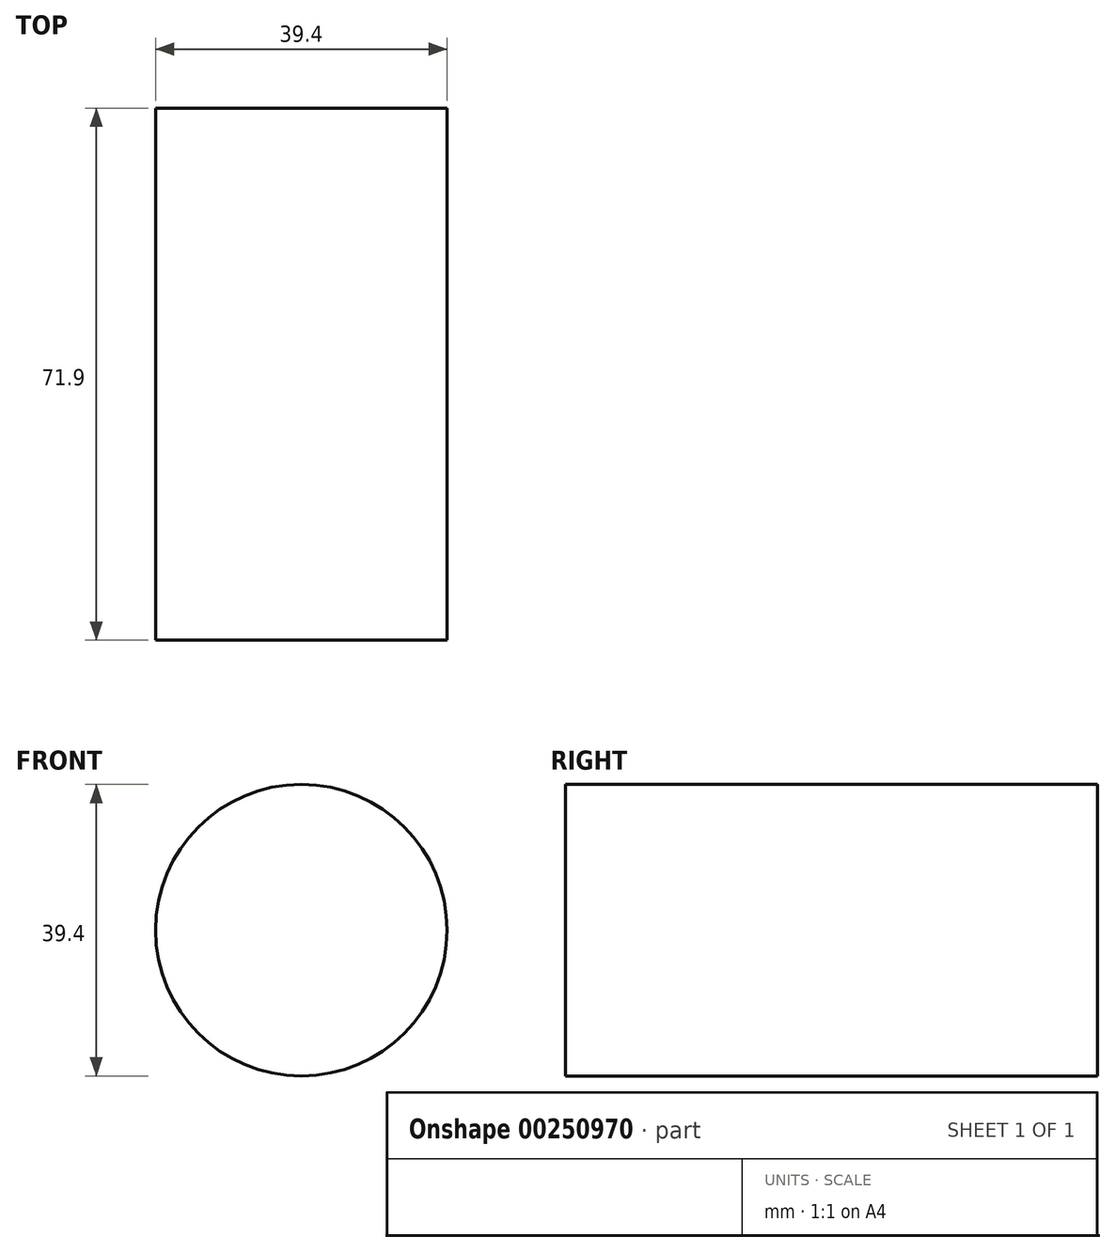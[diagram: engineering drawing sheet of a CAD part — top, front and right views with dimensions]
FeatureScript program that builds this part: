
annotation { "Feature Type Name" : "Feature", "Feature Type Description" : "" }
export const myFeature = defineFeature(function(context is Context, id is Id, definition is map)
    precondition{}
    {
        {
            var Q0;
            Q0=qCreatedBy(makeId("Front.planeOp"),FACE);
            var sketch = newSketch(context, id + "F0", { "sketchPlane" : qUnion([Q0])});
            skCircle(sketch, "E0", {"center": v(0, 0) * mm, "radius": 19.7 * mm});
            skSolve(sketch);
        }
        {
            var Q0;
            Q0=sQuery(id+"F0.wireOp",EDGE,"E0");
            extrude(context, id + "F1", {"bodyType" : ToolBodyType.SURFACE, "surfaceEntities" : qUnion([Q0]), "depth" : 71.9 * mm});
        }
    });
